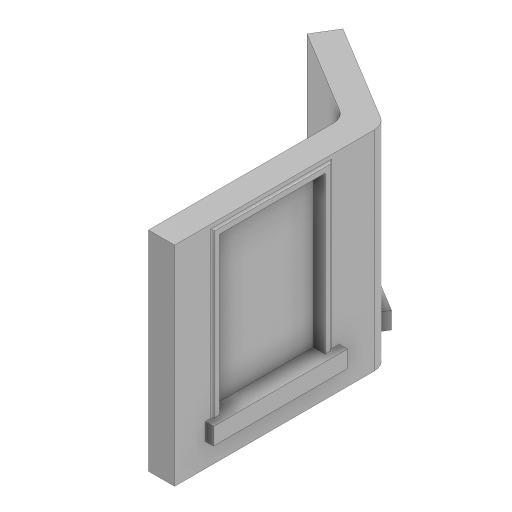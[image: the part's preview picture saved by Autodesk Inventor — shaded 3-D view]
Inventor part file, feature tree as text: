
AUTODESK INVENTOR PART (.ipt)
format: ipt  version: 2023 (Build 270158000, 158)  size: 285,696 bytes
history: native  units: in
note: dims shown in document units (in); Inventor stores cm internally (conversion verified against a paired STEP export)
features: extrude x8, sketch x8, projected_geometry x8, fillet x4, plane x1
ambient origin geometry x8: Origin, YZ Plane, XZ Plane, XY Plane, X Axis, Y Axis, Z Axis, Center Point
bodies: Solid1 (feature_tree)
feature tree (29):
  extrude  "Extrusion1"  Depth=157.4803in
  extrude  "Extrusion4"  Depth=19.685in
  fillet  "Fillet2"  Radius=2.0in
  fillet  "Fillet3"  Radius=12.0in
  fillet  "Fillet4"  Radius=9.8425in
  extrude  "Extrusion5"  Depth=39.3701in TaperAngle=0.0deg
  plane  "Work Plane3"
  extrude  "Extrusion6"  [1 undecoded]
  extrude  "Extrusion7"  Depth=1.0in TaperAngle=0.0deg
  extrude  "Extrusion8"  Depth=1.0in TaperAngle=0.0deg
  fillet  "Fillet5"  Radius=2.0in
  extrude  "Extrusion9"  Depth=6.0in TaperAngle=0.0deg
  extrude  "Extrusion10"  [1 undecoded]
  sketch  "Sketch1"  dims[d0=19.685in d1=157.4803in]
  sketch  "Sketch2"  dims[d2=118.1102in d3=0.0in d18=19.685in d19=2.0in d20=0.0in d21=12.0in d22=9.8425in]
  projected_geometry  "Projected Loop1"
  sketch  "Sketch4"  dims[d23=9.8425in d24=39.3701in d25=0.0in]
  projected_geometry  "Projected Loop3"
  sketch  "Sketch5"  dims[d26=118.1102in d27=0.0in d28=-30.5625in]
  projected_geometry  "Projected Loop4"
  sketch  "Sketch6"  dims[d29=4.0in d30=1.0in d31=0.0in]
  projected_geometry  "Projected Loop5"
  sketch  "Sketch7"  dims[d32=4.0in d33=1.0in d34=0.0in d35=2.0in]
  projected_geometry  "Projected Loop6"
  sketch  "Sketch8"  dims[d36=6.0in d37=0.0in d38=6.0in d39=0.0in]
  projected_geometry  "Projected Loop7"
  sketch  "Sketch9"
  projected_geometry  "Projected Loop8"
  projected_geometry  "Projected Loop9"
note: 2 required parameter values undecoded (feature->parameter linkage not recoverable at this tier; creation-order binding heuristic only, values carry confidence <= 0.55)
